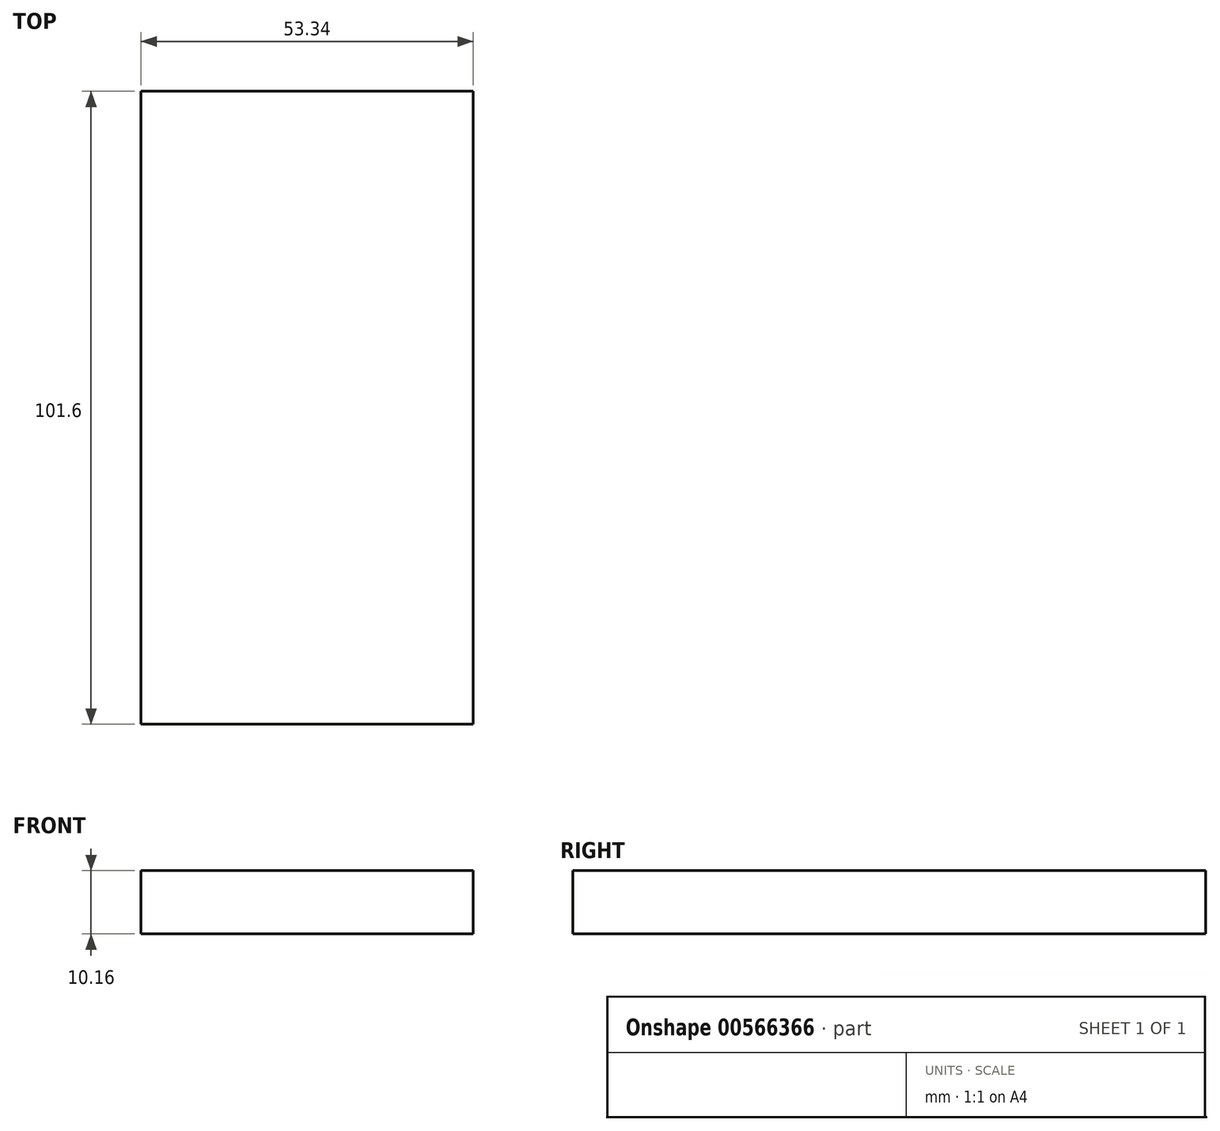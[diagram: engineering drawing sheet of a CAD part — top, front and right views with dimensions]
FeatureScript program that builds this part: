
annotation { "Feature Type Name" : "Feature", "Feature Type Description" : "" }
export const myFeature = defineFeature(function(context is Context, id is Id, definition is map)
    precondition{}
    {
        {
            var Q0;
            Q0=qCreatedBy(makeId("Top.planeOp"),FACE);
            var sketch = newSketch(context, id + "F0", { "sketchPlane" : qUnion([Q0])});
            skLineSegment(sketch, "E0.bottom", {"start": v(26.67, -50.8) * mm, "end": v(-26.67, -50.8) * mm});
            skLineSegment(sketch, "E0.top", {"start": v(26.67, 50.8) * mm, "end": v(-26.67, 50.8) * mm});
            skLineSegment(sketch, "E0.left", {"start": v(26.67, -50.8) * mm, "end": v(26.67, 50.8) * mm});
            skLineSegment(sketch, "E0.right", {"start": v(-26.67, -50.8) * mm, "end": v(-26.67, 50.8) * mm});
            skPoint(sketch, "E0.middle", {"position": v(0, 0) * mm});
            skSolve(sketch);
        }
        {
            var Q0;
            Q0=makeQuery(id+"F0.imprint","IMPRINT",FACE,{"disambiguationData":[TD([[makeQuery(id+"F0.imprint","IMPRINT",EDGE,{"derivedFrom":sQuery(id+"F0.wireOp",EDGE,"E0.bottom")}),-1.0]])]});
            extrude(context, id + "F1", {"entities" : qUnion([Q0]), "depth" : 10.16 * mm, "offsetDistance" : 25.4 * mm});
        }
    });
